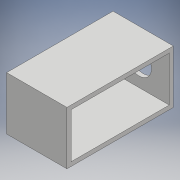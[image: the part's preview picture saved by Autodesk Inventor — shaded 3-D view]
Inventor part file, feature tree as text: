
AUTODESK INVENTOR PART (.ipt)
format: ipt  version: 2018 (Build 220112000, 112)  size: 104,448 bytes
history: native  units: mm
features: extrude x2, sketch x2, other x1
ambient origin geometry x8: Origin, YZ Plane, XZ Plane, XY Plane, X Axis, Y Axis, Z Axis, Center Point
bodies: Body1 (feature_tree)
feature tree (5):
  other  "ソリッド1"
  extrude  "押し出し1"  Depth=60.0mm
  extrude  "押し出し2"  Depth=30.0mm
  sketch  "スケッチ1"
  sketch  "スケッチ2"
